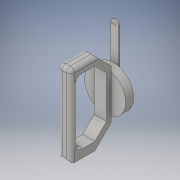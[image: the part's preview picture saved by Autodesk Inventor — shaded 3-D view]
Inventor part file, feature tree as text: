
AUTODESK INVENTOR PART (.ipt)
format: ipt  version: 2016 (Build 200138000, 138)  size: 204,288 bytes
history: native  units: mm
features: extrude x6, sketch x6, fillet x2, chamfer x1
ambient origin geometry x8: Origin, YZ Plane, XZ Plane, XY Plane, X Axis, Y Axis, Z Axis, Center Point
bodies: Solid1 (feature_tree)
feature tree (15):
  extrude  "Extrusion1"  Depth=20.0mm TaperAngle=0.0deg
  extrude  "Extrusion2"  Depth=200.0mm
  chamfer  "Chamfer1"  Distance=100.0mm
  extrude  "Extrusion3"  Depth=20.0mm
  fillet  "Fillet1"  Radius=20.0mm
  extrude  "Extrusion4"  Depth=20.0mm
  extrude  "Extrusion5"  TaperAngle=45.0deg  [1 undecoded]
  extrude  "Extrusion6"  Depth=10.0mm
  fillet  "Fillet2"  Radius=20.0mm
  sketch  "Sketch1"  dims[d0=100.0mm d1=20.0mm d2=0.0mm]
  sketch  "Sketch2"  dims[d5=100.0mm d6=200.0mm d7=100.0mm d8=0.0mm]
  sketch  "Sketch3"  dims[d9=40.0mm d10=2.0mm d11=45.0deg d12=20.0mm d13=20.0mm]
  sketch  "Sketch4"  dims[d14=20.0mm d15=40.0mm]
  sketch  "Sketch5"  dims[d16=135.0deg d17=45.0deg]
  sketch  "Sketch6"  dims[d18=100.0mm d19=0.0mm d20=10.0mm d21=20.0mm d22=3.0mm d23=0.0mm d25=20.0mm d28=3.0mm d29=0.0mm d31=50.0mm d32=3.0mm d33=3.0mm d34=0.0mm d35=10.0mm]
note: 1 required parameter value undecoded (feature->parameter linkage not recoverable at this tier; creation-order binding heuristic only, values carry confidence <= 0.55)
